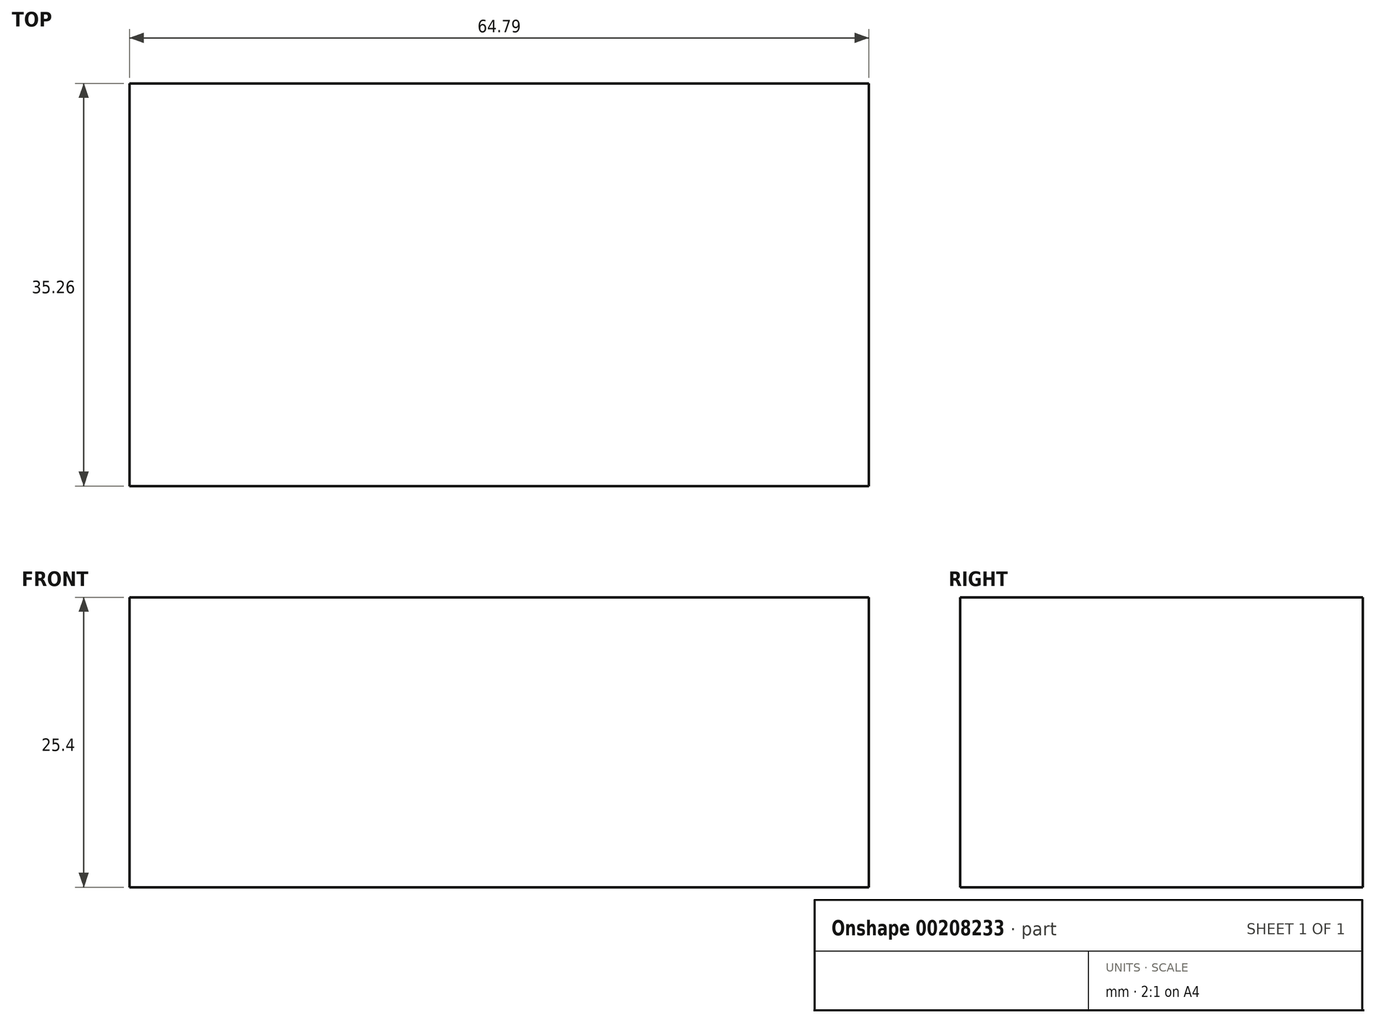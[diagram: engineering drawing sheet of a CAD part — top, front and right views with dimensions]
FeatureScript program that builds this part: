
annotation { "Feature Type Name" : "Feature", "Feature Type Description" : "" }
export const myFeature = defineFeature(function(context is Context, id is Id, definition is map)
    precondition{}
    {
        {
            var Q0;
            Q0=qCreatedBy(makeId("Top.planeOp"),FACE);
            var sketch = newSketch(context, id + "F0", { "sketchPlane" : qUnion([Q0])});
            skLineSegment(sketch, "E0.bottom", {"start": v(-26.52, 12.5) * mm, "end": v(38.27, 12.5) * mm});
            skLineSegment(sketch, "E0.top", {"start": v(-26.52, -22.75) * mm, "end": v(38.27, -22.75) * mm});
            skLineSegment(sketch, "E0.left", {"start": v(-26.52, 12.5) * mm, "end": v(-26.52, -22.75) * mm});
            skLineSegment(sketch, "E0.right", {"start": v(38.27, 12.5) * mm, "end": v(38.27, -22.75) * mm});
            skSolve(sketch);
        }
        {
            var Q0;
            Q0=makeQuery(id+"F0.imprint","IMPRINT",FACE,{"disambiguationData":[TD([[makeQuery(id+"F0.imprint","IMPRINT",EDGE,{"derivedFrom":sQuery(id+"F0.wireOp",EDGE,"E0.bottom")}),-1.0]])]});
            extrude(context, id + "F1", {"entities" : qUnion([Q0]), "depth" : 25.4 * mm});
        }
    });
